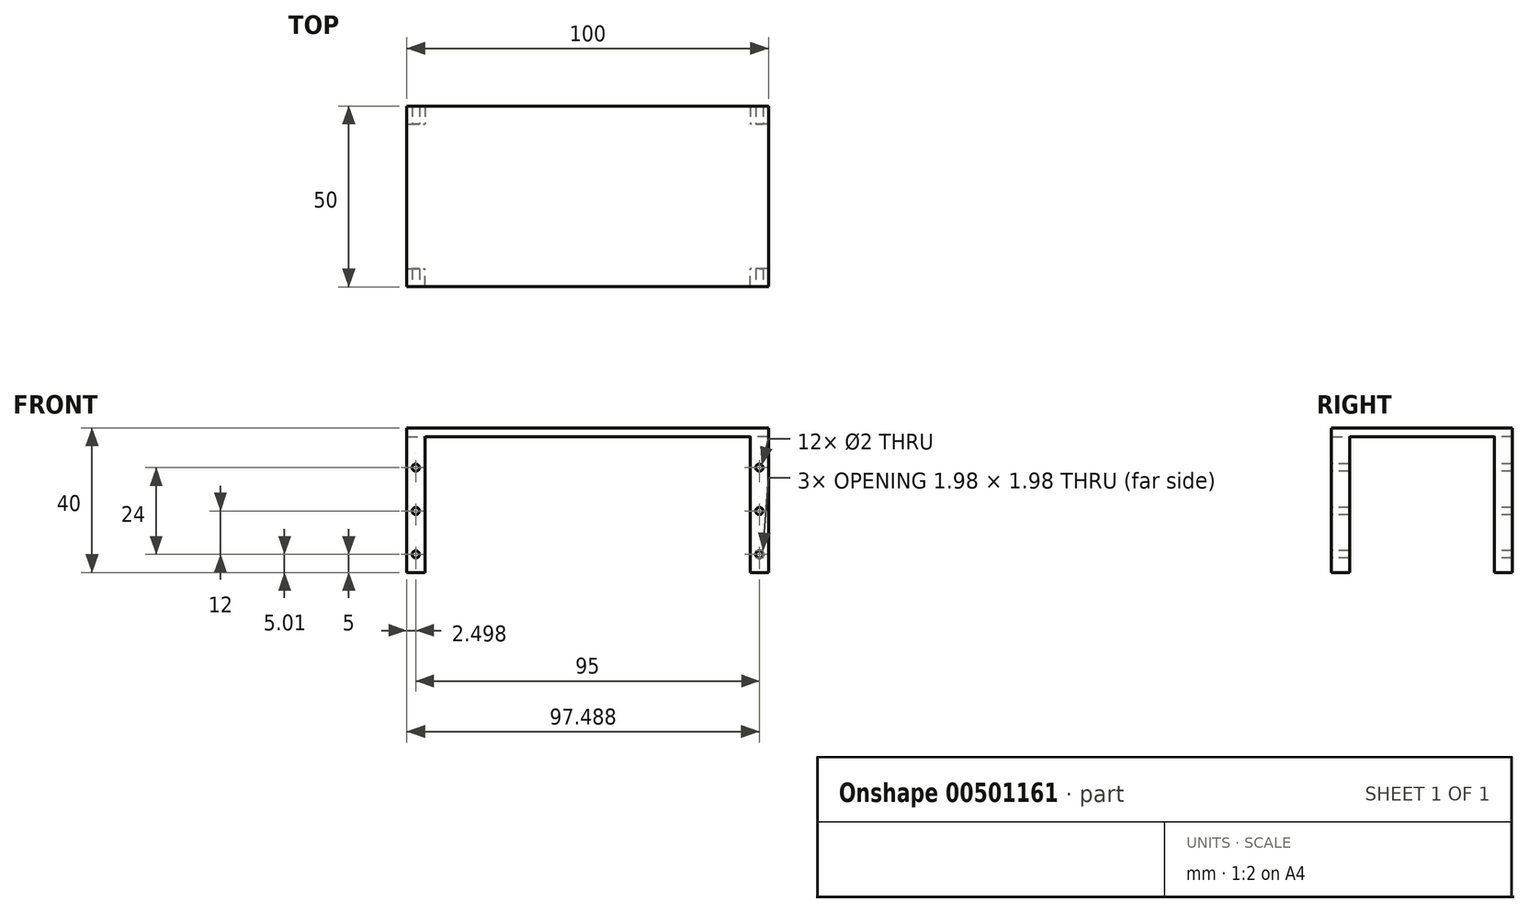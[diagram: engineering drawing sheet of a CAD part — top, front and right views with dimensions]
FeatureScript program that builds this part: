
annotation { "Feature Type Name" : "Feature", "Feature Type Description" : "" }
export const myFeature = defineFeature(function(context is Context, id is Id, definition is map)
    precondition{}
    {
        {
            var Q0;
            Q0=qCreatedBy(makeId("Top.planeOp"),FACE);
            var sketch = newSketch(context, id + "F0", { "sketchPlane" : qUnion([Q0])});
            skLineSegment(sketch, "E0.bottom", {"start": v(-51.15, -52.42) * mm, "end": v(48.85, -52.42) * mm});
            skLineSegment(sketch, "E0.top", {"start": v(-51.15, -2.42) * mm, "end": v(48.85, -2.42) * mm});
            skLineSegment(sketch, "E0.left", {"start": v(-51.15, -52.42) * mm, "end": v(-51.15, -2.42) * mm});
            skLineSegment(sketch, "E0.right", {"start": v(48.85, -52.42) * mm, "end": v(48.85, -2.42) * mm});
            skSolve(sketch);
        }
        {
            var Q0;
            Q0 = qSketchRegion(id + "F0", true);
            extrude(context, id + "F1", {"entities" : qUnion([Q0]), "depth" : 2.5 * mm});
        }
        {
            var Q0;
            Q0=makeQuery(id+"F1.opExtrude","CAP_FACE",FACE,{"disambiguationData":[OSD([sQuery(id+"F0.wireOp",EDGE,"E0.bottom"),sQuery(id+"F0.wireOp",EDGE,"E0.top"),sQuery(id+"F0.wireOp",EDGE,"E0.left"),sQuery(id+"F0.wireOp",EDGE,"E0.right")])],"isStart":false});
            var sketch = newSketch(context, id + "F2", { "sketchPlane" : qUnion([Q0])});
            skLineSegment(sketch, "E1.bottom", {"start": v(-51.15, -2.42) * mm, "end": v(-46.15, -2.42) * mm});
            skLineSegment(sketch, "E1.top", {"start": v(-51.15, -7.42) * mm, "end": v(-46.15, -7.42) * mm});
            skLineSegment(sketch, "E1.left", {"start": v(-51.15, -2.42) * mm, "end": v(-51.15, -7.42) * mm});
            skLineSegment(sketch, "E1.right", {"start": v(-46.15, -2.42) * mm, "end": v(-46.15, -7.42) * mm});
            skLineSegment(sketch, "E2.bottom", {"start": v(48.85, -2.42) * mm, "end": v(43.85, -2.42) * mm});
            skLineSegment(sketch, "E2.top", {"start": v(48.85, -7.42) * mm, "end": v(43.85, -7.42) * mm});
            skLineSegment(sketch, "E2.left", {"start": v(48.85, -2.42) * mm, "end": v(48.85, -7.42) * mm});
            skLineSegment(sketch, "E2.right", {"start": v(43.85, -2.42) * mm, "end": v(43.85, -7.42) * mm});
            skLineSegment(sketch, "E3.bottom", {"start": v(48.85, -52.42) * mm, "end": v(43.85, -52.42) * mm});
            skLineSegment(sketch, "E3.top", {"start": v(48.85, -47.42) * mm, "end": v(43.85, -47.42) * mm});
            skLineSegment(sketch, "E3.left", {"start": v(48.85, -52.42) * mm, "end": v(48.85, -47.42) * mm});
            skLineSegment(sketch, "E3.right", {"start": v(43.85, -52.42) * mm, "end": v(43.85, -47.42) * mm});
            skLineSegment(sketch, "E4.bottom", {"start": v(-51.15, -52.42) * mm, "end": v(-46.15, -52.42) * mm});
            skLineSegment(sketch, "E4.top", {"start": v(-51.15, -47.42) * mm, "end": v(-46.15, -47.42) * mm});
            skLineSegment(sketch, "E4.left", {"start": v(-51.15, -52.42) * mm, "end": v(-51.15, -47.42) * mm});
            skLineSegment(sketch, "E4.right", {"start": v(-46.15, -52.42) * mm, "end": v(-46.15, -47.42) * mm});
            skSolve(sketch);
        }
        {
            var Q0;
            Q0 = qSketchRegion(id + "F2", true);
            extrude(context, id + "F3", {"entities" : qUnion([Q0]), "operationType" : NewBodyOperationType.ADD, "oppositeDirection" : true, "depth" : 40 * mm});
        }
        {
            var Q0;
            Q0=makeQuery(id+"F3.boolean.opBoolean","MERGE",FACE,{"derivedFrom":[makeQuery(id+"F1.opExtrude","SWEPT_FACE",FACE,{"disambiguationData":[OSD([sQuery(id+"F0.wireOp",EDGE,"E0.bottom")])]}),makeQuery(id+"F3.opExtrude","SWEPT_FACE",FACE,{"disambiguationData":[OSD([sQuery(id+"F2.wireOp",EDGE,"E3.bottom")])]}),makeQuery(id+"F3.opExtrude","SWEPT_FACE",FACE,{"disambiguationData":[OSD([sQuery(id+"F2.wireOp",EDGE,"E4.bottom")])]})]});
            var sketch = newSketch(context, id + "F4", { "sketchPlane" : qUnion([Q0])});
            skCircle(sketch, "E5", {"center": v(46.35, -32.5) * mm, "radius": 1 * mm});
            skCircle(sketch, "E6", {"center": v(46.35, -20.5) * mm, "radius": 1 * mm});
            skCircle(sketch, "E7", {"center": v(46.35, -8.5) * mm, "radius": 1 * mm});
            skCircle(sketch, "E8", {"center": v(-48.65, -8.5) * mm, "radius": 1 * mm});
            skCircle(sketch, "E9", {"center": v(-48.65, -20.5) * mm, "radius": 1 * mm});
            skCircle(sketch, "E10", {"center": v(-48.65, -32.5) * mm, "radius": 1 * mm});
            skSolve(sketch);
        }
        {
            var Q0;
            Q0 = qSketchRegion(id + "F4", true);
            extrude(context, id + "F5", {"entities" : qUnion([Q0]), "operationType" : NewBodyOperationType.REMOVE, "endBound" : BoundingType.THROUGH_ALL, "oppositeDirection" : true, "depth" : 25 * mm});
        }
    });
